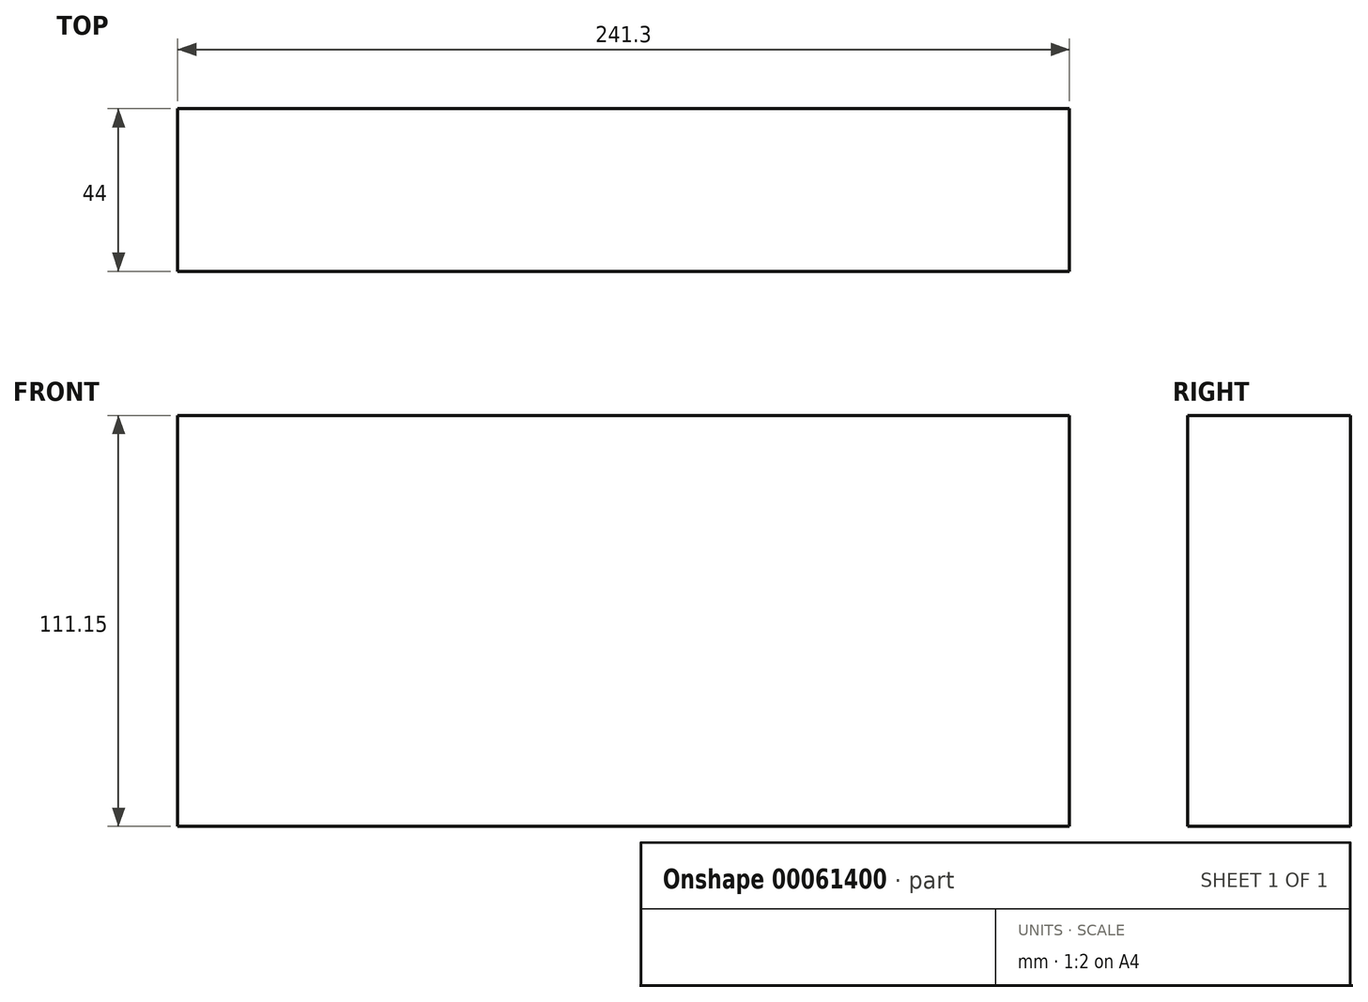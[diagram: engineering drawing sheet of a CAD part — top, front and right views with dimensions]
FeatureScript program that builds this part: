
annotation { "Feature Type Name" : "Feature", "Feature Type Description" : "" }
export const myFeature = defineFeature(function(context is Context, id is Id, definition is map)
    precondition{}
    {
        {
            var Q0;
            Q0=qCreatedBy(makeId("Front.planeOp"),FACE);
            var sketch = newSketch(context, id + "F0", { "sketchPlane" : qUnion([Q0])});
            skLineSegment(sketch, "E0.bottom", {"start": v(0, 0) * mm, "end": v(-241.3, 0) * mm});
            skLineSegment(sketch, "E0.top", {"start": v(0, 111.15) * mm, "end": v(-241.3, 111.15) * mm});
            skLineSegment(sketch, "E0.left", {"start": v(0, 0) * mm, "end": v(0, 111.15) * mm});
            skLineSegment(sketch, "E0.right", {"start": v(-241.3, 0) * mm, "end": v(-241.3, 111.15) * mm});
            skSolve(sketch);
        }
        {
            var Q0;
            Q0 = qSketchRegion(id + "F0", true);
            extrude(context, id + "F1", {"entities" : qUnion([Q0]), "depth" : 44 * mm});
        }
    });
